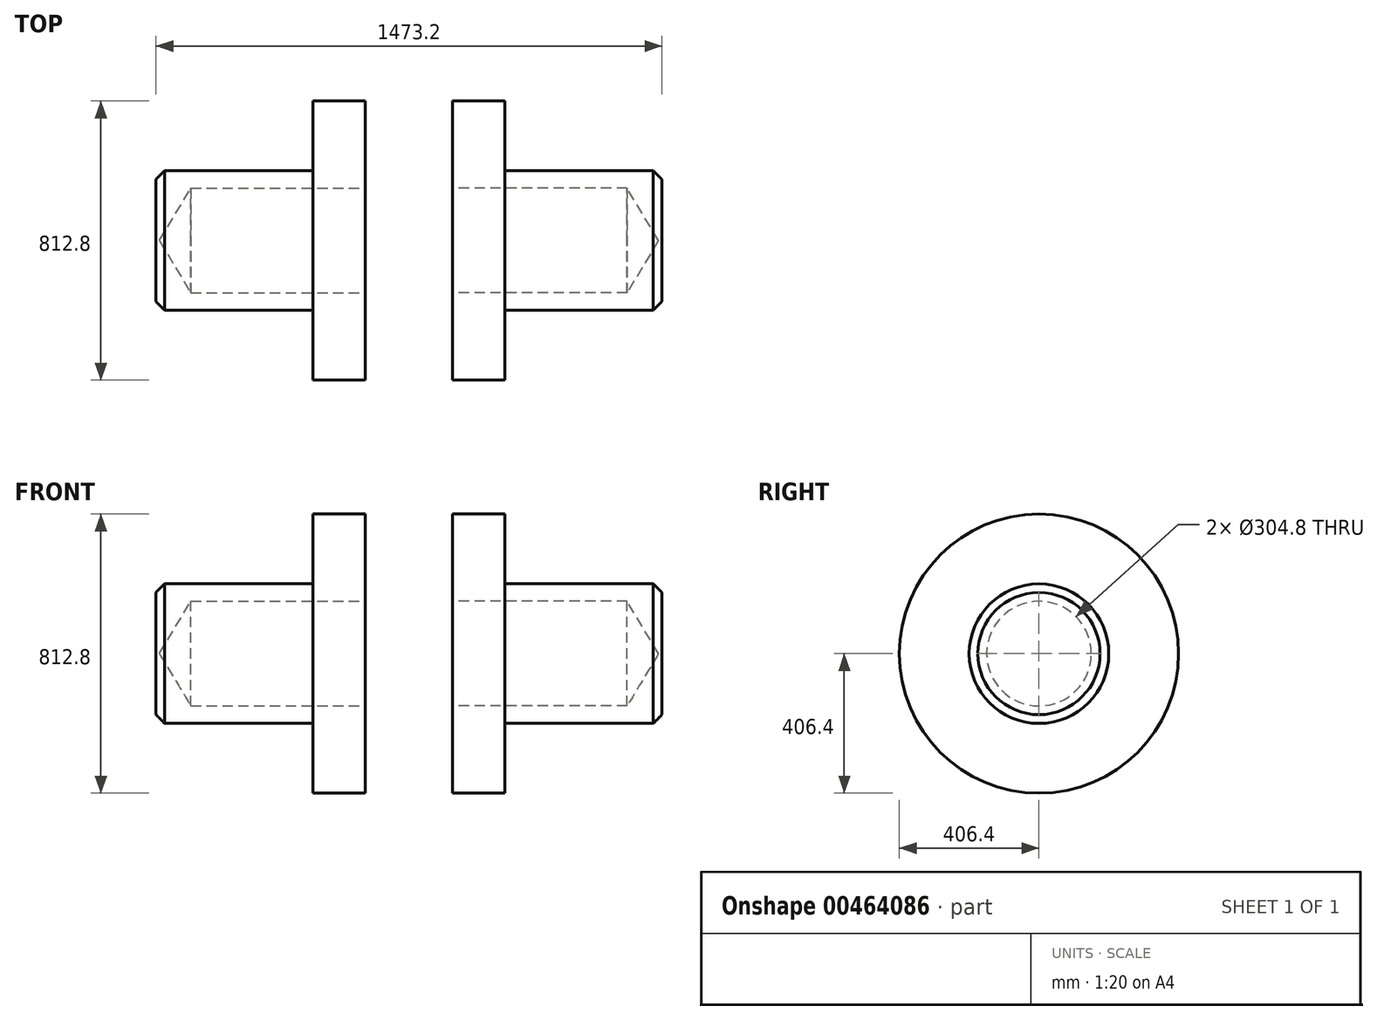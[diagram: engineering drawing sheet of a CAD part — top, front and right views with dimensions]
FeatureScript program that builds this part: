
annotation { "Feature Type Name" : "Feature", "Feature Type Description" : "" }
export const myFeature = defineFeature(function(context is Context, id is Id, definition is map)
    precondition{}
    {
        {
            var Q0;
            Q0=qCreatedBy(makeId("Right.planeOp"),FACE);
            var sketch = newSketch(context, id + "F0", { "sketchPlane" : qUnion([Q0])});
            skCircle(sketch, "E0", {"center": v(0, 0) * mm, "radius": 406.4 * mm});
            skCircle(sketch, "E1", {"center": v(0, 0) * mm, "radius": 203.2 * mm});
            skSolve(sketch);
        }
        {
            var Q0;
            Q0=makeQuery(id+"F0.imprint","IMPRINT",FACE,{"disambiguationData":[TD([[makeQuery(id+"F0.imprint","IMPRINT",EDGE,{"derivedFrom":sQuery(id+"F0.wireOp",EDGE,"M601LQcb-G6mk-X1rX-goBj-z7MNnR4HHchU")}),1.0]])]});
            var Q1;
            Q1=makeQuery(id+"F0.imprint","IMPRINT",FACE,{"disambiguationData":[TD([[makeQuery(id+"F0.imprint","IMPRINT",EDGE,{"derivedFrom":sQuery(id+"F0.wireOp",EDGE,"E1")}),1.0]])]});
            extrude(context, id + "F1", {"entities" : qUnion([Q0, Q1]), "oppositeDirection" : true, "depth" : 609.6 * mm});
        }
        {
            var Q0;
            Q0=makeQuery(id+"F1.opExtrude","CAP_FACE",FACE,{"disambiguationData":[OSD([sQuery(id+"F0.wireOp",EDGE,"E1")])],"isStart":true});
            var sketch = newSketch(context, id + "F2", { "sketchPlane" : qUnion([Q0])});
            skCircle(sketch, "E2", {"center": v(0, 0) * mm, "radius": 152.4 * mm});
            skSolve(sketch);
        }
        {
            var Q0;
            Q0=sQuery(id+"F2.wireOp",VERTEX,"E2.center");
            var Q1;
            Q1=makeQuery(id+"F1.opExtrude","SWEPT_BODY",BODY,{"disambiguationData":[OSD([sQuery(id+"F0.wireOp",EDGE,"E1")])]});
            hole(context, id + "F3", {"style" : HoleStyle.SIMPLE, "endStyle" : HoleEndStyle.BLIND, "holeDiameter" : 304.8 * mm, "holeDepth" : 508 * mm, "isTappedThrough" : true, "tappedDepth" : 12.7 * mm, "tapClearance" : 3, "locations" : qUnion([Q0]), "scope" : qUnion([Q1])});
        }
        {
            var Q0;
            Q0=makeQuery(id+"F0.imprint","IMPRINT",FACE,{"disambiguationData":[TD([[makeQuery(id+"F0.imprint","IMPRINT",EDGE,{"derivedFrom":sQuery(id+"F0.wireOp",EDGE,"E0")}),1.0]])]});
            extrude(context, id + "F4", {"entities" : qUnion([Q0]), "operationType" : NewBodyOperationType.ADD, "oppositeDirection" : true, "depth" : 152.4 * mm});
        }
        {
            var Q0;
            Q0=makeQuery(id+"F1.opExtrude","CAP_EDGE",EDGE,{"disambiguationData":[OSD([sQuery(id+"F0.wireOp",EDGE,"E1")])],"isStart":false});
            chamfer(context, id + "F5", {"entities" : qUnion([Q0]), "chamferType" : ChamferType.OFFSET_ANGLE, "width" : 25.4 * mm, "oppositeDirection" : false, "angle" : 45 * degree, "tangentPropagation" : true});
        }
        {
            var Q0;
            Q0=makeQuery(id+"F0.imprint","IMPRINT",FACE,{"disambiguationData":[TD([[makeQuery(id+"F0.imprint","IMPRINT",EDGE,{"derivedFrom":sQuery(id+"F0.wireOp",EDGE,"E0")}),1.0]])]});
            cPlane(context, id + "F6", {"entities" : qUnion([Q0]), "cplaneType" : CPlaneType.OFFSET, "offset" : 127 * mm, "width" : 152.4 * mm, "height" : 152.4 * mm});
        }
        {
            var Q0;
            Q0=makeQuery(id+"F1.opExtrude","SWEPT_BODY",BODY,{"disambiguationData":[OSD([sQuery(id+"F0.wireOp",EDGE,"E1")])]});
            var Q1;
            Q1=qCreatedBy(id+"F6.planeOp",FACE);
            mirror(context, id + "F7", {"entities" : qUnion([Q0]), "mirrorPlane" : qUnion([Q1])});
        }
    });
